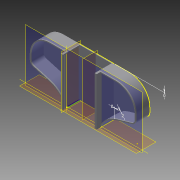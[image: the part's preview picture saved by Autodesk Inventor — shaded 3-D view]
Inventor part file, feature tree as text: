
AUTODESK INVENTOR PART (.ipt)
format: ipt  version: 2015 (Build 190159000, 159)  size: 333,312 bytes
history: native  units: mm
features: sketch x13, extrude x12, projected_geometry x8, mirror x5, plane x2
ambient origin geometry x8: Origin, YZ Plane, XZ Plane, XY Plane, X Axis, Y Axis, Z Axis, Center Point
bodies: Solid1 (feature_tree)
feature tree (40):
  extrude  "Extrusion1"  Depth=2.0mm
  sketch  "Sketch2"  dims[d2=64.0mm d3=2.0mm]
  extrude  "Extrusion3"  Depth=2.0mm
  sketch  "Sketch6"  dims[d6=2.0mm d7=2.0mm]
  extrude  "Extrusion4"  Depth=2.0mm
  extrude  "Extrusion5"  Depth=2.0mm
  plane  "Work Plane1"
  mirror  "Mirror1"
  mirror  "Mirror2"
  extrude  "Extrusion6"  Depth=2.0mm
  extrude  "Extrusion7"  Depth=96.5mm TaperAngle=0.0deg
  mirror  "Mirror3"
  sketch  "Sketch10"  dims[d18=40.0mm d20=50.0mm]
  sketch  "Sketch11"  dims[d21=10.0mm d22=2.0mm d23=0.0mm]
  sketch  "Sketch12"  dims[d24=0.0mm d25=0.0mm]
  extrude  "Extrusion10"  Depth=50.0mm
  extrude  "Extrusion11"  Depth=2.0mm TaperAngle=0.0deg
  mirror  "Mirror5"
  mirror  "Mirror6"
  extrude  "Extrusion12"  TaperAngle=0.0deg  [1 undecoded]
  extrude  "Extrusion13"  Depth=2.0mm TaperAngle=0.0deg
  extrude  "Extrusion14"  Depth=2.0mm TaperAngle=0.0deg
  extrude  "Extrusion15"  Depth=2.0mm
  sketch  "Sketch1"  dims[d0=24.0mm d1=2.0mm]
  projected_geometry  "Projected Loop1"
  sketch  "Sketch5"  dims[d4=24.0mm d5=2.0mm]
  projected_geometry  "Projected Loop2"
  projected_geometry  "Projected Loop3"
  sketch  "Sketch8"  dims[d8=2.0mm d9=2.0mm]
  projected_geometry  "Projected Loop4"
  sketch  "Sketch9"  dims[d10=2.0mm d11=96.5mm d12=0.0mm]
  plane  "Work Plane2"
  projected_geometry  "Projected Loop6"
  sketch  "Sketch13"  dims[d26=2.0mm d27=2.0mm d28=0.0mm]
  projected_geometry  "Projected Loop7"
  projected_geometry  "Projected Loop8"
  sketch  "Sketch14"  dims[d29=2.0mm d30=0.0mm d31=2.0mm d32=0.0mm]
  projected_geometry  "Projected Loop9"
  sketch  "Sketch15"  dims[d33=2.0mm d34=0.0mm d35=2.0mm]
  sketch  "Sketch16"  dims[d36=2.0mm d37=2.0mm d38=4.0mm d43=2.0mm d44=0.0mm d45=2.0mm d46=0.0mm d47=2.0mm d48=0.0mm d49=2.0mm d50=2.0mm d51=2.0mm d52=4.0mm d53=2.0mm d54=0.0mm d55=2.0mm d56=0.0mm d57=2.0mm d58=0.0mm]
note: 1 required parameter value undecoded (feature->parameter linkage not recoverable at this tier; creation-order binding heuristic only, values carry confidence <= 0.55)
